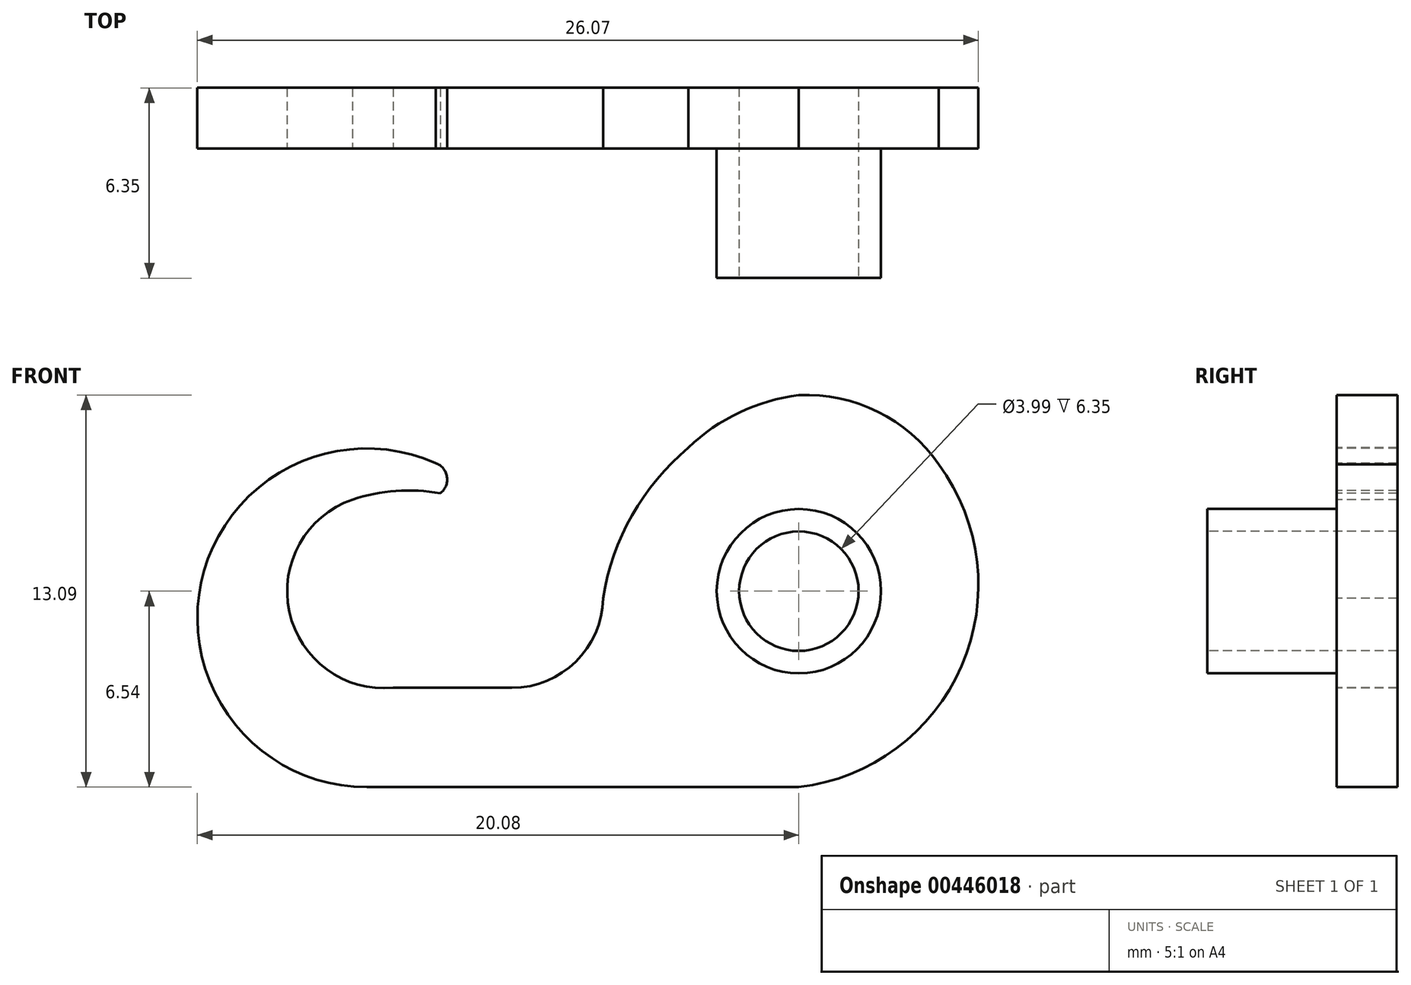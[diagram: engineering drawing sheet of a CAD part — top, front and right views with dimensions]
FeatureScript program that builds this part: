
annotation { "Feature Type Name" : "Feature", "Feature Type Description" : "" }
export const myFeature = defineFeature(function(context is Context, id is Id, definition is map)
    precondition{}
    {
        {
            var Q0;
            Q0=qCreatedBy(makeId("Front.planeOp"),FACE);
            var sketch = newSketch(context, id + "F0", { "sketchPlane" : qUnion([Q0])});
            skArc(sketch, "E0", {"start": v(-6.54, 0) * mm, "mid": v(-6.54, -0.12) * mm, "end": v(-6.54, -0.24) * mm});
            skArc(sketch, "E1", {"start": v(-14.9, 3.06) * mm, "mid": v(-17, -0.69) * mm, "end": v(-13.54, -3.22) * mm});
            skLineSegment(sketch, "E2", {"start": v(0, -6.54) * mm, "end": v(-14.43, -6.54) * mm});
            skLineSegment(sketch, "E3", {"start": v(-13.54, -3.22) * mm, "end": v(-9.58, -3.22) * mm});
            skArc(sketch, "E4", {"start": v(-9.58, -3.22) * mm, "mid": v(-7.37, -2.27) * mm, "end": v(-6.54, 0) * mm});
            skCircle(sketch, "E5", {"center": v(0, 0) * mm, "radius": 2 * mm});
            skArc(sketch, "E6", {"start": v(-11.97, 3.27) * mm, "mid": v(-13.45, 3.35) * mm, "end": v(-14.9, 3.06) * mm});
            skArc(sketch, "E7", {"start": v(-2, 5.87) * mm, "mid": v(-5.03, 3.37) * mm, "end": v(-6.54, -0.24) * mm});
            skPoint(sketch, "E8.orphan", {"position": v(0, 6.54) * mm});
            skPoint(sketch, "E9", {"position": v(6.54, 0) * mm});
            skPoint(sketch, "E10", {"position": v(-13.89, 3.3) * mm});
            skPoint(sketch, "E11", {"position": v(-19.1, 0) * mm});
            skPoint(sketch, "E12", {"position": v(-17.08, 0) * mm});
            skPoint(sketch, "E13", {"position": v(-13.84, 4.73) * mm});
            skArc(sketch, "E14", {"start": v(-11.97, 3.27) * mm, "mid": v(-11.75, 3.82) * mm, "end": v(-12.13, 4.27) * mm});
            skPoint(sketch, "E15", {"position": v(-12.05, 3.22) * mm});
            skPoint(sketch, "E16", {"position": v(-6.27, 0.93) * mm});
            skArc(sketch, "E17", {"start": v(0, -6.54) * mm, "mid": v(5.43, -2.5) * mm, "end": v(4.67, 4.23) * mm});
            skPoint(sketch, "E18", {"position": v(5.99, 0) * mm});
            skArc(sketch, "E19", {"start": v(-12.13, 4.27) * mm, "mid": v(-19.96, 0.29) * mm, "end": v(-14.43, -6.54) * mm});
            skPoint(sketch, "E20", {"position": v(-20.08, -0.75) * mm});
            skArc(sketch, "E21", {"start": v(0, 6.54) * mm, "mid": v(-1.99, 5.97) * mm, "end": v(-3.69, 4.79) * mm});
            skArc(sketch, "E22", {"start": v(4.67, 4.23) * mm, "mid": v(2.63, 6) * mm, "end": v(0, 6.54) * mm});
            skLineSegment(sketch, "E23", {"start": v(5.99, 0) * mm, "end": v(-7.04, 0) * mm, "construction": true});
            skSolve(sketch);
        }
        {
            var Q0;
            Q0=makeQuery(id+"F0.imprint","IMPRINT",FACE,{"disambiguationData":[TD([[makeQuery(id+"F0.imprint","IMPRINT",EDGE,{"derivedFrom":sQuery(id+"F0.wireOp",EDGE,"E1")}),-1.0]])]});
            extrude(context, id + "F1", {"entities" : qUnion([Q0]), "oppositeDirection" : true, "depth" : 2.03 * mm});
        }
        {
            var Q0;
            Q0=makeQuery(id+"F1.opExtrude","CAP_FACE",FACE,{"disambiguationData":[OSD([sQuery(id+"F0.wireOp",EDGE,"E1"),sQuery(id+"F0.wireOp",EDGE,"E2"),sQuery(id+"F0.wireOp",EDGE,"E3"),sQuery(id+"F0.wireOp",EDGE,"E4"),sQuery(id+"F0.wireOp",EDGE,"1ggT3jzS-p47a-YT00-n6m3-NP0iiMOPYwaf"),sQuery(id+"F0.wireOp",EDGE,"UBbcAXa3-V91W-9m4f-UJa9-hQQzLGmEDhn6"),sQuery(id+"F0.wireOp",EDGE,"JgP3Zjv9-m9wI-iaQm-6L1D-HzGFGdHjzEY5"),sQuery(id+"F0.wireOp",EDGE,"E5"),sQuery(id+"F0.wireOp",EDGE,"ZZPeETQD-BKMX-CuAd-HruW-VI17b69Nytd4")])],"isStart":true});
            var sketch = newSketch(context, id + "F2", { "sketchPlane" : qUnion([Q0])});
            skCircle(sketch, "E24", {"center": v(0, 0) * mm, "radius": 2.74 * mm});
            skSolve(sketch);
        }
        {
            var Q0;
            Q0=makeQuery(id+"F2.imprint","IMPRINT",FACE,{"disambiguationData":[TD([[makeQuery(id+"F2.imprint","IMPRINT",EDGE,{"derivedFrom":sQuery(id+"F2.wireOp",EDGE,"E24")}),1.0]])]});
            extrude(context, id + "F3", {"entities" : qUnion([Q0]), "operationType" : NewBodyOperationType.ADD, "depth" : 4.32 * mm});
        }
    });
